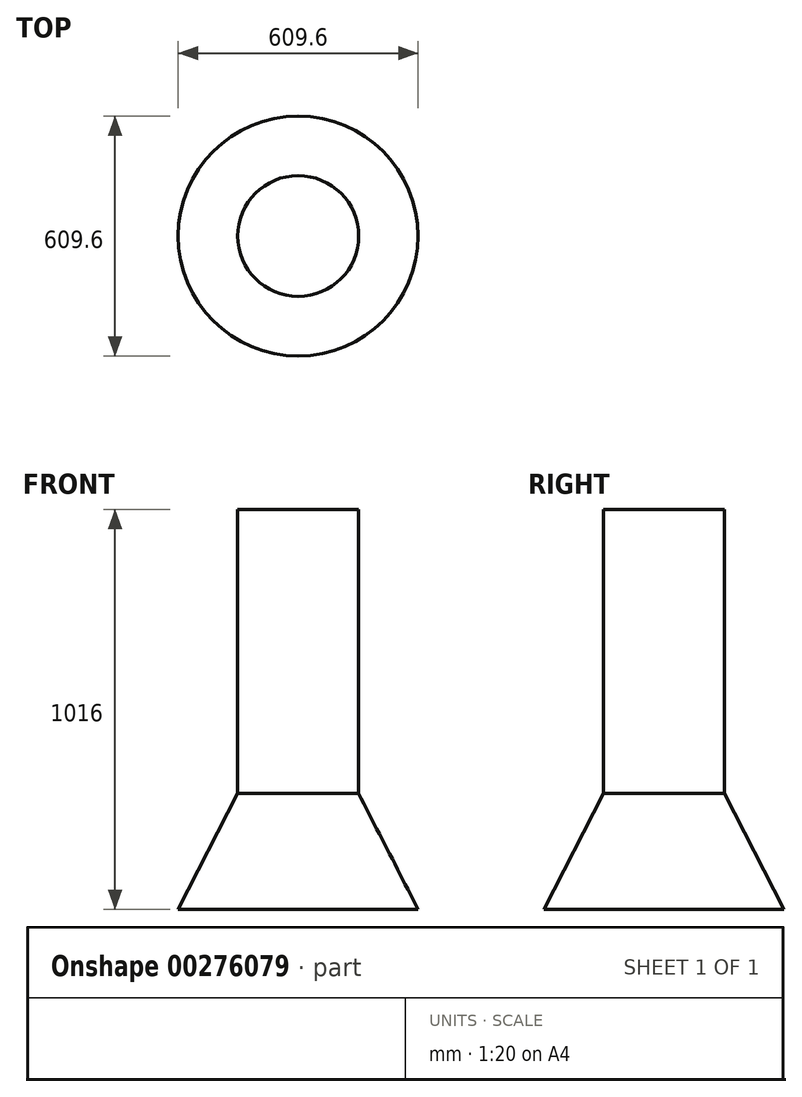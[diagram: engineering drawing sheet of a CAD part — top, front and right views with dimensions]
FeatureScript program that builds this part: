
annotation { "Feature Type Name" : "Feature", "Feature Type Description" : "" }
export const myFeature = defineFeature(function(context is Context, id is Id, definition is map)
    precondition{}
    {
        {
            var Q0;
            Q0=qCreatedBy(makeId("Front.planeOp"),FACE);
            var sketch = newSketch(context, id + "F0", { "sketchPlane" : qUnion([Q0])});
            skLineSegment(sketch, "E0", {"start": v(0, 0) * mm, "end": v(304.8, 0) * mm});
            skLineSegment(sketch, "E1", {"start": v(304.8, 0) * mm, "end": v(153.59, 294.21) * mm});
            skLineSegment(sketch, "E2", {"start": v(153.59, 294.21) * mm, "end": v(153.59, 1016) * mm});
            skLineSegment(sketch, "E3", {"start": v(153.59, 1016) * mm, "end": v(0, 1016) * mm});
            skLineSegment(sketch, "E4", {"start": v(0, 1016) * mm, "end": v(0, 0) * mm});
            skSolve(sketch);
        }
        {
            var Q0;
            Q0 = qSketchRegion(id + "F0", true);
            var Q1;
            Q1=sQuery(id+"F0.wireOp",EDGE,"E4");
            revolve(context, id + "F1", {"entities" : qUnion([Q0]), "axis" : qUnion([Q1]), "revolveType" : RevolveType.FULL});
        }
    });
